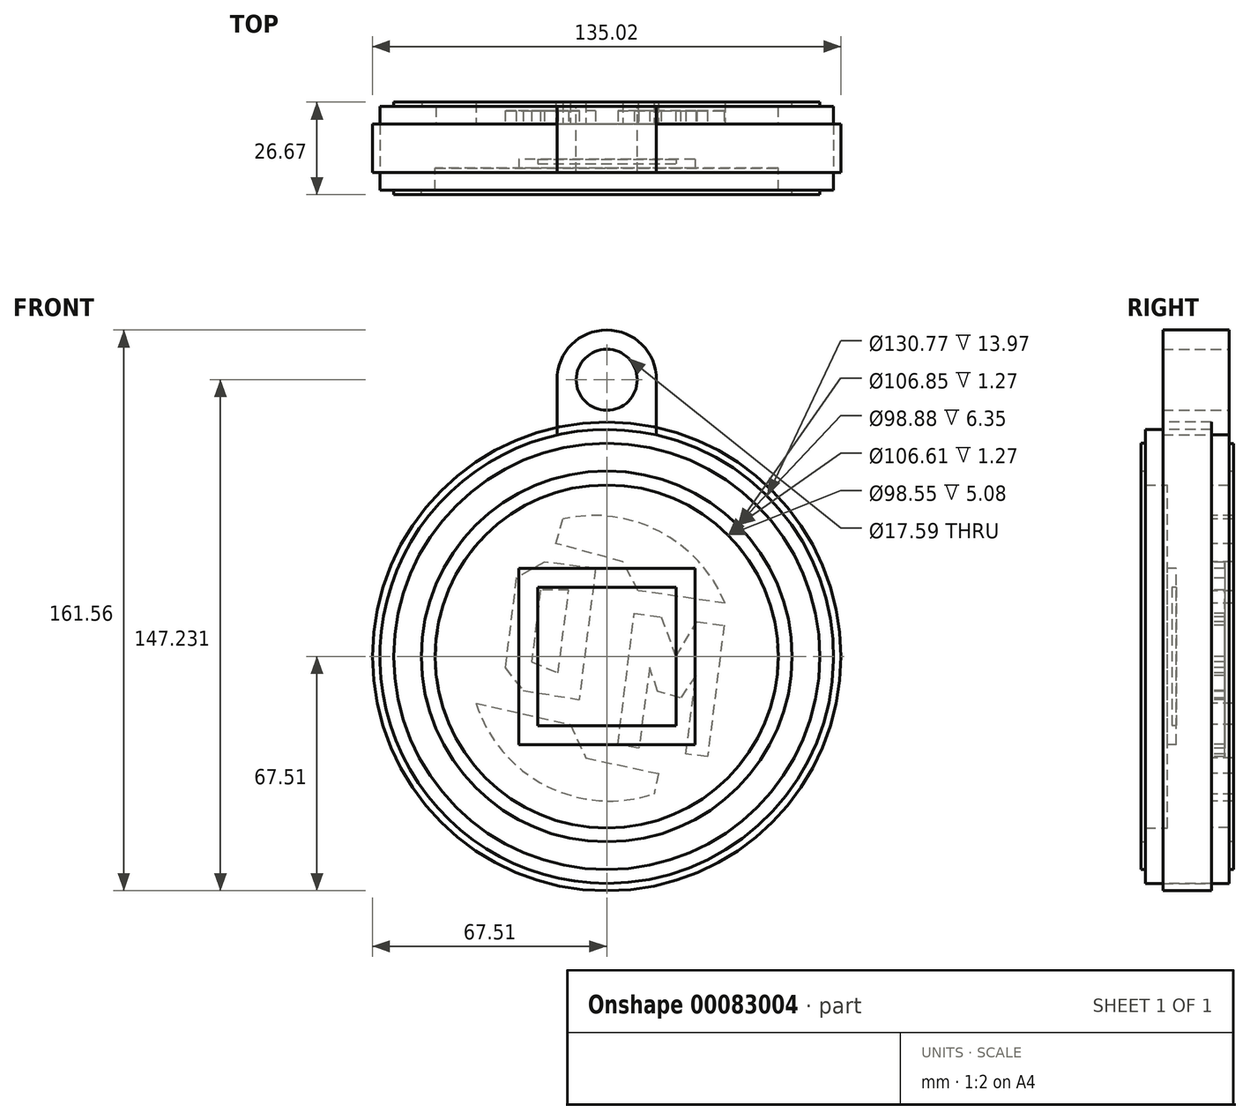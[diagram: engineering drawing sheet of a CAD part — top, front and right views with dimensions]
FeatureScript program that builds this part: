
annotation { "Feature Type Name" : "Feature", "Feature Type Description" : "" }
export const myFeature = defineFeature(function(context is Context, id is Id, definition is map)
    precondition{}
    {
        {
            var Q0;
            Q0=qCreatedBy(makeId("Front.planeOp"),FACE);
            var sketch = newSketch(context, id + "F0", { "sketchPlane" : qUnion([Q0])});
            skCircle(sketch, "E0", {"center": v(0, 0) * mm, "radius": 65.39 * mm});
            skCircle(sketch, "E1", {"center": v(0, 0) * mm, "radius": 49.28 * mm});
            skSolve(sketch);
        }
        {
            var Q0;
            Q0=makeQuery(id+"F0.imprint","IMPRINT",FACE,{"disambiguationData":[TD([[makeQuery(id+"F0.imprint","IMPRINT",EDGE,{"derivedFrom":sQuery(id+"F0.wireOp",EDGE,"E1")}),1.0]])]});
            var Q1;
            Q1=makeQuery(id+"F0.imprint","IMPRINT",FACE,{"disambiguationData":[TD([[makeQuery(id+"F0.imprint","IMPRINT",EDGE,{"derivedFrom":sQuery(id+"F0.wireOp",EDGE,"E0")}),1.0]])]});
            extrude(context, id + "F1", {"entities" : qUnion([Q0, Q1]), "depth" : 12.7 * mm});
        }
        {
            var Q0;
            Q0=makeQuery(id+"F0.imprint","IMPRINT",FACE,{"disambiguationData":[TD([[makeQuery(id+"F0.imprint","IMPRINT",EDGE,{"derivedFrom":sQuery(id+"F0.wireOp",EDGE,"E0")}),1.0]])]});
            extrude(context, id + "F2", {"entities" : qUnion([Q0]), "operationType" : NewBodyOperationType.ADD, "oppositeDirection" : true, "depth" : 5.08 * mm});
        }
        {
            var Q0;
            Q0=makeQuery(id+"F1.opExtrude","CAP_FACE",FACE,{"disambiguationData":[OSD([sQuery(id+"F0.wireOp",EDGE,"E0")])],"isStart":false});
            var sketch = newSketch(context, id + "F3", { "sketchPlane" : qUnion([Q0])});
            skCircle(sketch, "E2", {"center": v(0, 0) * mm, "radius": 49.44 * mm});
            skSolve(sketch);
        }
        {
            var Q0;
            Q0=makeQuery(id+"F3.imprint","IMPRINT",FACE,{"disambiguationData":[TD([[makeQuery(id+"F3.imprint","IMPRINT",EDGE,{"derivedFrom":sQuery(id+"F3.wireOp",EDGE,"E2")}),-1.0]])]});
            extrude(context, id + "F4", {"entities" : qUnion([Q0]), "operationType" : NewBodyOperationType.ADD, "depth" : 6.35 * mm});
        }
        {
            var Q0;
            Q0=makeQuery(id+"F4.opExtrude","CAP_FACE",FACE,{"disambiguationData":[OSD([sQuery(id+"F0.wireOp",EDGE,"E0"),sQuery(id+"F3.wireOp",EDGE,"E2")])],"isStart":false});
            var sketch = newSketch(context, id + "F5", { "sketchPlane" : qUnion([Q0])});
            skLineSegment(sketch, "E3", {"start": v(0, 49.44) * mm, "end": v(0, 65.39) * mm});
            skPoint(sketch, "E4", {"position": v(0, 57.41) * mm});
            skLineSegment(sketch, "E5", {"start": v(0, 57.41) * mm, "end": v(0, 65.39) * mm});
            skLineSegment(sketch, "E6", {"start": v(0, 49.44) * mm, "end": v(0, 57.41) * mm});
            skPoint(sketch, "E7", {"position": v(0, 53.43) * mm});
            skPoint(sketch, "E8", {"position": v(0, 61.4) * mm});
            skCircle(sketch, "E9", {"center": v(0, 0) * mm, "radius": 53.43 * mm});
            skCircle(sketch, "E10", {"center": v(0, 0) * mm, "radius": 61.4 * mm});
            skSolve(sketch);
        }
        {
            var Q0;
            Q0=makeQuery(id+"F5.imprint","IMPRINT",FACE,{"disambiguationData":[TD([[makeQuery(id+"F5.imprint","IMPRINT",EDGE,{"derivedFrom":sQuery(id+"F5.wireOp",EDGE,"E9")}),-1.0]])]});
            extrude(context, id + "F6", {"entities" : qUnion([Q0]), "operationType" : NewBodyOperationType.ADD, "depth" : 1.27 * mm});
        }
        {
            var Q0;
            Q0=makeQuery(id+"F2.opExtrude","CAP_FACE",FACE,{"disambiguationData":[OSD([sQuery(id+"F0.wireOp",EDGE,"E0"),sQuery(id+"F0.wireOp",EDGE,"E1")])],"isStart":false});
            var sketch = newSketch(context, id + "F7", { "sketchPlane" : qUnion([Q0])});
            skLineSegment(sketch, "E11", {"start": v(0, 49.28) * mm, "end": v(0, 65.39) * mm});
            skPoint(sketch, "E12", {"position": v(0, 57.33) * mm});
            skLineSegment(sketch, "E13", {"start": v(0, 57.33) * mm, "end": v(0, 65.39) * mm});
            skLineSegment(sketch, "E14", {"start": v(0, 57.33) * mm, "end": v(0, 49.28) * mm});
            skPoint(sketch, "E15", {"position": v(0, 61.36) * mm});
            skPoint(sketch, "E16", {"position": v(0, 53.3) * mm});
            skCircle(sketch, "E17", {"center": v(0, 0) * mm, "radius": 53.3 * mm});
            skCircle(sketch, "E18", {"center": v(0, 0) * mm, "radius": 61.36 * mm});
            skSolve(sketch);
        }
        {
            var Q0;
            Q0=makeQuery(id+"F7.imprint","IMPRINT",FACE,{"disambiguationData":[TD([[makeQuery(id+"F7.imprint","IMPRINT",EDGE,{"derivedFrom":sQuery(id+"F7.wireOp",EDGE,"E17")}),-1.0]])]});
            extrude(context, id + "F8", {"entities" : qUnion([Q0]), "operationType" : NewBodyOperationType.ADD, "depth" : 1.27 * mm});
        }
        {
            var Q0;
            Q0=makeQuery(id+"F0.imprint","IMPRINT",FACE,{"disambiguationData":[TD([[makeQuery(id+"F0.imprint","IMPRINT",EDGE,{"derivedFrom":sQuery(id+"F0.wireOp",EDGE,"E1")}),1.0]])]});
            var sketch = newSketch(context, id + "F9", { "sketchPlane" : qUnion([Q0])});
            skLineSegment(sketch, "E19", {"start": v(0, 0) * mm, "end": v(6.38, 0) * mm});
            skLineSegment(sketch, "E20", {"start": v(0, 0) * mm, "end": v(-6.38, 0) * mm});
            skLineSegment(sketch, "E21", {"start": v(6.38, 0) * mm, "end": v(3.19, -25.35) * mm});
            skPoint(sketch, "E21.endSnap0", {"position": v(3.19, 0) * mm});
            skLineSegment(sketch, "E22", {"start": v(-6.38, 0) * mm, "end": v(-3.19, 25.35) * mm});
            skPoint(sketch, "E22.endSnap0", {"position": v(-3.19, 0) * mm});
            skLineSegment(sketch, "E23", {"start": v(6.38, 0) * mm, "end": v(7.93, 12.37) * mm});
            skLineSegment(sketch, "E24", {"start": v(-6.38, 0) * mm, "end": v(-7.94, -12.42) * mm});
            skLineSegment(sketch, "E25", {"start": v(7.93, 12.37) * mm, "end": v(15.7, 11.4) * mm});
            skLineSegment(sketch, "E26", {"start": v(15.7, 11.4) * mm, "end": v(19.92, 0) * mm});
            skLineSegment(sketch, "E27", {"start": v(19.92, 0) * mm, "end": v(25.93, 10) * mm});
            skLineSegment(sketch, "E28", {"start": v(25.93, 10) * mm, "end": v(33.82, 9) * mm});
            skLineSegment(sketch, "E29", {"start": v(33.82, 9) * mm, "end": v(29.05, -28.9) * mm});
            skLineSegment(sketch, "E30", {"start": v(29.05, -28.9) * mm, "end": v(22.84, -28.11) * mm});
            skLineSegment(sketch, "E31", {"start": v(22.84, -28.11) * mm, "end": v(25.68, -5.55) * mm});
            skLineSegment(sketch, "E32", {"start": v(25.68, -5.55) * mm, "end": v(21.28, -11.93) * mm});
            skLineSegment(sketch, "E33", {"start": v(21.28, -11.93) * mm, "end": v(14.68, -10) * mm});
            skLineSegment(sketch, "E34", {"start": v(14.68, -10) * mm, "end": v(12.35, -3.2) * mm});
            skLineSegment(sketch, "E35", {"start": v(12.35, -3.2) * mm, "end": v(9.24, -26.49) * mm});
            skLineSegment(sketch, "E36", {"start": v(9.24, -26.49) * mm, "end": v(3.19, -25.35) * mm});
            skLineSegment(sketch, "E37", {"start": v(-3.19, 25.35) * mm, "end": v(-17.93, 27.2) * mm});
            skLineSegment(sketch, "E38", {"start": v(-17.93, 27.2) * mm, "end": v(-26.08, 22.6) * mm});
            skLineSegment(sketch, "E39", {"start": v(-26.08, 22.6) * mm, "end": v(-29.33, -3.23) * mm});
            skLineSegment(sketch, "E40", {"start": v(-29.33, -3.23) * mm, "end": v(-24.14, -9.8) * mm});
            skLineSegment(sketch, "E41", {"start": v(-24.14, -9.8) * mm, "end": v(-7.94, -12.42) * mm});
            skLineSegment(sketch, "E42", {"start": v(-10.94, 19.12) * mm, "end": v(-19.09, 19.12) * mm});
            skLineSegment(sketch, "E43", {"start": v(-19.09, 19.12) * mm, "end": v(-21.68, -1.5) * mm});
            skLineSegment(sketch, "E44", {"start": v(-21.68, -1.5) * mm, "end": v(-14.04, -4.75) * mm});
            skLineSegment(sketch, "E45", {"start": v(-14.04, -4.75) * mm, "end": v(-10.94, 19.12) * mm});
            skSolve(sketch);
        }
        {
            var Q0;
            Q0 = qSketchRegion(id + "F9", true);
            extrude(context, id + "F10", {"entities" : qUnion([Q0]), "operationType" : NewBodyOperationType.ADD, "oppositeDirection" : true, "depth" : 3.8 * mm});
        }
        {
            var Q0;
            Q0=makeQuery(id+"F1.opExtrude","CAP_FACE",FACE,{"disambiguationData":[OSD([sQuery(id+"F0.wireOp",EDGE,"E0")])],"isStart":false});
            var sketch = newSketch(context, id + "F11", { "sketchPlane" : qUnion([Q0])});
            skLineSegment(sketch, "E46.bottom", {"start": v(0, 0) * mm, "end": v(-25.4, 0) * mm});
            skLineSegment(sketch, "E46.top", {"start": v(0, 25.4) * mm, "end": v(-25.4, 25.4) * mm});
            skLineSegment(sketch, "E46.left", {"start": v(0, 0) * mm, "end": v(0, 25.4) * mm});
            skLineSegment(sketch, "E46.right", {"start": v(-25.4, 0) * mm, "end": v(-25.4, 25.4) * mm});
            skLineSegment(sketch, "E47.MirrorCS", {"start": v(25.4, 0) * mm, "end": v(25.4, 25.4) * mm});
            skLineSegment(sketch, "E48.MirrorCS", {"start": v(0, 25.4) * mm, "end": v(25.4, 25.4) * mm});
            skLineSegment(sketch, "E49.MirrorCS", {"start": v(0, 0) * mm, "end": v(25.4, 0) * mm});
            skLineSegment(sketch, "E50.MirrorCS", {"start": v(-25.4, 0) * mm, "end": v(-25.4, -25.4) * mm});
            skLineSegment(sketch, "E51.MirrorCS", {"start": v(0, -25.4) * mm, "end": v(-25.4, -25.4) * mm});
            skLineSegment(sketch, "E52.MirrorCS", {"start": v(0, -25.4) * mm, "end": v(25.4, -25.4) * mm});
            skLineSegment(sketch, "E53.MirrorCS", {"start": v(25.4, 0) * mm, "end": v(25.4, -25.4) * mm});
            skLineSegment(sketch, "E54.MirrorCS", {"start": v(0, 0) * mm, "end": v(0, -25.4) * mm});
            skPoint(sketch, "E55", {"position": v(-12.7, 12.7) * mm});
            skPoint(sketch, "E55.positionSnap0", {"position": v(-25.4, 12.7) * mm});
            skPoint(sketch, "E55.positionSnap1", {"position": v(-12.7, 25.4) * mm});
            skPoint(sketch, "E56", {"position": v(12.7, 12.7) * mm});
            skPoint(sketch, "E56.positionSnap0", {"position": v(25.4, 12.7) * mm});
            skPoint(sketch, "E56.positionSnap1", {"position": v(12.7, 25.4) * mm});
            skPoint(sketch, "E57", {"position": v(-12.7, -12.7) * mm});
            skPoint(sketch, "E57.positionSnap0", {"position": v(-12.7, -25.4) * mm});
            skPoint(sketch, "E57.positionSnap1", {"position": v(0, -12.7) * mm});
            skPoint(sketch, "E58", {"position": v(12.7, -12.7) * mm});
            skPoint(sketch, "E58.positionSnap0", {"position": v(12.7, -25.4) * mm});
            skPoint(sketch, "E58.positionSnap1", {"position": v(25.4, -12.7) * mm});
            skLineSegment(sketch, "E59.bottom", {"start": v(-12.7, 12.7) * mm, "end": v(12.7, 12.7) * mm});
            skLineSegment(sketch, "E59.top", {"start": v(-12.7, -12.7) * mm, "end": v(12.7, -12.7) * mm});
            skLineSegment(sketch, "E59.left", {"start": v(-12.7, 12.7) * mm, "end": v(-12.7, -12.7) * mm});
            skLineSegment(sketch, "E59.right", {"start": v(12.7, 12.7) * mm, "end": v(12.7, -12.7) * mm});
            skLineSegment(sketch, "E60", {"start": v(-12.7, 12.7) * mm, "end": v(-12.7, 25.4) * mm});
            skLineSegment(sketch, "E61", {"start": v(-25.4, 12.7) * mm, "end": v(-12.7, 12.7) * mm});
            skLineSegment(sketch, "E62", {"start": v(12.7, 12.7) * mm, "end": v(12.7, 25.4) * mm});
            skLineSegment(sketch, "E63", {"start": v(12.7, 12.7) * mm, "end": v(25.4, 12.7) * mm});
            skLineSegment(sketch, "E64", {"start": v(12.7, -25.4) * mm, "end": v(12.7, -12.7) * mm});
            skLineSegment(sketch, "E65", {"start": v(12.7, -12.7) * mm, "end": v(25.4, -12.7) * mm});
            skLineSegment(sketch, "E66", {"start": v(-12.7, -12.7) * mm, "end": v(-12.7, -25.4) * mm});
            skLineSegment(sketch, "E67", {"start": v(-12.7, -12.7) * mm, "end": v(-25.4, -12.7) * mm});
            skPoint(sketch, "E68", {"position": v(-19.05, 19.05) * mm});
            skPoint(sketch, "E68.positionSnap0", {"position": v(-12.7, 19.05) * mm});
            skPoint(sketch, "E68.positionSnap1", {"position": v(-19.05, 12.7) * mm});
            skPoint(sketch, "E69", {"position": v(19.05, 19.05) * mm});
            skPoint(sketch, "E69.positionSnap0", {"position": v(12.7, 19.05) * mm});
            skPoint(sketch, "E69.positionSnap1", {"position": v(19.05, 12.7) * mm});
            skPoint(sketch, "E70", {"position": v(-19.05, -19.05) * mm});
            skPoint(sketch, "E70.positionSnap0", {"position": v(-19.05, -12.7) * mm});
            skPoint(sketch, "E70.positionSnap1", {"position": v(-12.7, -19.05) * mm});
            skPoint(sketch, "E71", {"position": v(19.05, -19.05) * mm});
            skPoint(sketch, "E71.positionSnap0", {"position": v(19.05, -12.7) * mm});
            skPoint(sketch, "E71.positionSnap1", {"position": v(12.7, -19.05) * mm});
            skLineSegment(sketch, "E72.bottom", {"start": v(-19.05, 19.05) * mm, "end": v(19.05, 19.05) * mm});
            skLineSegment(sketch, "E72.top", {"start": v(-19.05, -19.05) * mm, "end": v(19.05, -19.05) * mm});
            skLineSegment(sketch, "E72.left", {"start": v(-19.05, 19.05) * mm, "end": v(-19.05, -19.05) * mm});
            skLineSegment(sketch, "E72.right", {"start": v(19.05, 19.05) * mm, "end": v(19.05, -19.05) * mm});
            skSolve(sketch);
        }
        {
            var Q0;
            {var subQ1=sQuery(id+"F11.wireOp",EDGE,"E46.right");var subQ6=sQuery(id+"F11.wireOp",EDGE,"E46.top");var subQ10=makeQuery(id+"F11.imprint","INTERSECT",VERTEX,{"derivedFrom":[subQ6,subQ1]});Q0=makeQuery(id+"F11.imprint","IMPRINT",FACE,{"disambiguationData":[TD([[makeQuery(id+"F11.imprint","IMPRINT",EDGE,{"disambiguationData":[TD([[subQ10,1.0]])],"derivedFrom":subQ6}),1.0]])]});}
            var Q1;
            {var subQ3=sQuery(id+"F11.wireOp",EDGE,"E72.bottom");var subQ5=sQuery(id+"F11.wireOp",EDGE,"E72.left");var subQ6=makeQuery(id+"F11.imprint","INTERSECT",VERTEX,{"derivedFrom":[subQ3,subQ5]});Q1=makeQuery(id+"F11.imprint","IMPRINT",FACE,{"disambiguationData":[TD([[makeQuery(id+"F11.imprint","IMPRINT",EDGE,{"disambiguationData":[TD([[subQ6,-1.0]])],"derivedFrom":subQ3}),-1.0]])]});}
            var Q2;
            {var subQ0=sQuery(id+"F11.wireOp",EDGE,"E59.bottom");var subQ1=sQuery(id+"F11.wireOp",EDGE,"E46.left");var subQ2=makeQuery(id+"F11.imprint","INTERSECT",VERTEX,{"derivedFrom":[subQ1,subQ0]});Q2=makeQuery(id+"F11.imprint","IMPRINT",FACE,{"disambiguationData":[TD([[makeQuery(id+"F11.imprint","IMPRINT",EDGE,{"disambiguationData":[TD([[subQ2,-1.0]])],"derivedFrom":subQ1}),-1.0]])]});}
            var Q3;
            {var subQ0=sQuery(id+"F11.wireOp",EDGE,"E48.MirrorCS");var subQ5=sQuery(id+"F11.wireOp",EDGE,"E62");var subQ6=makeQuery(id+"F11.imprint","INTERSECT",VERTEX,{"derivedFrom":[subQ0,subQ5]});Q3=makeQuery(id+"F11.imprint","IMPRINT",FACE,{"disambiguationData":[TD([[makeQuery(id+"F11.imprint","IMPRINT",EDGE,{"disambiguationData":[TD([[subQ6,1.0]])],"derivedFrom":subQ5}),1.0]])]});}
            var Q4;
            {var subQ1=sQuery(id+"F11.wireOp",EDGE,"E46.top");var subQ3=sQuery(id+"F11.wireOp",EDGE,"E60");var subQ4=makeQuery(id+"F11.imprint","INTERSECT",VERTEX,{"derivedFrom":[subQ1,subQ3]});Q4=makeQuery(id+"F11.imprint","IMPRINT",FACE,{"disambiguationData":[TD([[makeQuery(id+"F11.imprint","IMPRINT",EDGE,{"disambiguationData":[TD([[subQ4,1.0]])],"derivedFrom":subQ3}),-1.0]])]});}
            var Q5;
            {var subQ0=sQuery(id+"F11.wireOp",EDGE,"E59.bottom");var subQ1=sQuery(id+"F11.wireOp",EDGE,"E46.left");var subQ2=makeQuery(id+"F11.imprint","INTERSECT",VERTEX,{"derivedFrom":[subQ1,subQ0]});Q5=makeQuery(id+"F11.imprint","IMPRINT",FACE,{"disambiguationData":[TD([[makeQuery(id+"F11.imprint","IMPRINT",EDGE,{"disambiguationData":[TD([[subQ2,-1.0]])],"derivedFrom":subQ1}),1.0]])]});}
            var Q6;
            {var subQ1=sQuery(id+"F11.wireOp",EDGE,"E46.bottom");var subQ3=sQuery(id+"F11.wireOp",EDGE,"E59.left");var subQ4=makeQuery(id+"F11.imprint","INTERSECT",VERTEX,{"derivedFrom":[subQ1,subQ3]});Q6=makeQuery(id+"F11.imprint","IMPRINT",FACE,{"disambiguationData":[TD([[makeQuery(id+"F11.imprint","IMPRINT",EDGE,{"disambiguationData":[TD([[subQ4,1.0]])],"derivedFrom":subQ1}),-1.0]])]});}
            var Q7;
            {var subQ0=sQuery(id+"F11.wireOp",EDGE,"E59.left");var subQ1=sQuery(id+"F11.wireOp",EDGE,"E46.bottom");var subQ2=makeQuery(id+"F11.imprint","INTERSECT",VERTEX,{"derivedFrom":[subQ1,subQ0]});Q7=makeQuery(id+"F11.imprint","IMPRINT",FACE,{"disambiguationData":[TD([[makeQuery(id+"F11.imprint","IMPRINT",EDGE,{"disambiguationData":[TD([[subQ2,-1.0]])],"derivedFrom":subQ1}),-1.0]])]});}
            var Q8;
            {var subQ0=sQuery(id+"F11.wireOp",EDGE,"E46.right");var subQ5=sQuery(id+"F11.wireOp",EDGE,"E61");var subQ6=makeQuery(id+"F11.imprint","INTERSECT",VERTEX,{"derivedFrom":[subQ0,subQ5]});Q8=makeQuery(id+"F11.imprint","IMPRINT",FACE,{"disambiguationData":[TD([[makeQuery(id+"F11.imprint","IMPRINT",EDGE,{"disambiguationData":[TD([[subQ6,-1.0]])],"derivedFrom":subQ5}),-1.0]])]});}
            var Q9;
            {var subQ0=sQuery(id+"F11.wireOp",EDGE,"E50.MirrorCS");var subQ5=sQuery(id+"F11.wireOp",EDGE,"E67");var subQ6=makeQuery(id+"F11.imprint","INTERSECT",VERTEX,{"derivedFrom":[subQ0,subQ5]});Q9=makeQuery(id+"F11.imprint","IMPRINT",FACE,{"disambiguationData":[TD([[makeQuery(id+"F11.imprint","IMPRINT",EDGE,{"disambiguationData":[TD([[subQ6,1.0]])],"derivedFrom":subQ5}),-1.0]])]});}
            var Q10;
            {var subQ0=sQuery(id+"F11.wireOp",EDGE,"E59.left");var subQ1=sQuery(id+"F11.wireOp",EDGE,"E46.bottom");var subQ2=makeQuery(id+"F11.imprint","INTERSECT",VERTEX,{"derivedFrom":[subQ1,subQ0]});Q10=makeQuery(id+"F11.imprint","IMPRINT",FACE,{"disambiguationData":[TD([[makeQuery(id+"F11.imprint","IMPRINT",EDGE,{"disambiguationData":[TD([[subQ2,-1.0]])],"derivedFrom":subQ1}),1.0]])]});}
            var Q11;
            {var subQ1=sQuery(id+"F11.wireOp",EDGE,"E46.bottom");var subQ3=sQuery(id+"F11.wireOp",EDGE,"E59.left");var subQ4=makeQuery(id+"F11.imprint","INTERSECT",VERTEX,{"derivedFrom":[subQ1,subQ3]});Q11=makeQuery(id+"F11.imprint","IMPRINT",FACE,{"disambiguationData":[TD([[makeQuery(id+"F11.imprint","IMPRINT",EDGE,{"disambiguationData":[TD([[subQ4,1.0]])],"derivedFrom":subQ1}),1.0]])]});}
            var Q12;
            {var subQ1=sQuery(id+"F11.wireOp",EDGE,"E49.MirrorCS");var subQ3=sQuery(id+"F11.wireOp",EDGE,"E59.right");var subQ4=makeQuery(id+"F11.imprint","INTERSECT",VERTEX,{"derivedFrom":[subQ1,subQ3]});Q12=makeQuery(id+"F11.imprint","IMPRINT",FACE,{"disambiguationData":[TD([[makeQuery(id+"F11.imprint","IMPRINT",EDGE,{"disambiguationData":[TD([[subQ4,1.0]])],"derivedFrom":subQ1}),-1.0]])]});}
            var Q13;
            {var subQ1=sQuery(id+"F11.wireOp",EDGE,"E46.left");var subQ3=sQuery(id+"F11.wireOp",EDGE,"E59.bottom");var subQ4=makeQuery(id+"F11.imprint","INTERSECT",VERTEX,{"derivedFrom":[subQ1,subQ3]});Q13=makeQuery(id+"F11.imprint","IMPRINT",FACE,{"disambiguationData":[TD([[makeQuery(id+"F11.imprint","IMPRINT",EDGE,{"disambiguationData":[TD([[subQ4,1.0]])],"derivedFrom":subQ1}),-1.0]])]});}
            var Q14;
            {var subQ0=sQuery(id+"F11.wireOp",EDGE,"E59.right");var subQ1=sQuery(id+"F11.wireOp",EDGE,"E49.MirrorCS");var subQ2=makeQuery(id+"F11.imprint","INTERSECT",VERTEX,{"derivedFrom":[subQ1,subQ0]});Q14=makeQuery(id+"F11.imprint","IMPRINT",FACE,{"disambiguationData":[TD([[makeQuery(id+"F11.imprint","IMPRINT",EDGE,{"disambiguationData":[TD([[subQ2,-1.0]])],"derivedFrom":subQ1}),1.0]])]});}
            var Q15;
            {var subQ1=sQuery(id+"F11.wireOp",EDGE,"E47.MirrorCS");var subQ3=sQuery(id+"F11.wireOp",EDGE,"E63");var subQ4=makeQuery(id+"F11.imprint","INTERSECT",VERTEX,{"derivedFrom":[subQ1,subQ3]});Q15=makeQuery(id+"F11.imprint","IMPRINT",FACE,{"disambiguationData":[TD([[makeQuery(id+"F11.imprint","IMPRINT",EDGE,{"disambiguationData":[TD([[subQ4,1.0]])],"derivedFrom":subQ3}),-1.0]])]});}
            var Q16;
            {var subQ1=sQuery(id+"F11.wireOp",EDGE,"E47.MirrorCS");var subQ5=sQuery(id+"F11.wireOp",EDGE,"E48.MirrorCS");var subQ6=makeQuery(id+"F11.imprint","INTERSECT",VERTEX,{"derivedFrom":[subQ1,subQ5]});Q16=makeQuery(id+"F11.imprint","IMPRINT",FACE,{"disambiguationData":[TD([[makeQuery(id+"F11.imprint","IMPRINT",EDGE,{"disambiguationData":[TD([[subQ6,1.0]])],"derivedFrom":subQ1}),1.0]])]});}
            var Q17;
            {var subQ3=sQuery(id+"F11.wireOp",EDGE,"E72.bottom");var subQ5=sQuery(id+"F11.wireOp",EDGE,"E72.right");var subQ7=makeQuery(id+"F11.imprint","INTERSECT",VERTEX,{"derivedFrom":[subQ3,subQ5]});Q17=makeQuery(id+"F11.imprint","IMPRINT",FACE,{"disambiguationData":[TD([[makeQuery(id+"F11.imprint","IMPRINT",EDGE,{"disambiguationData":[TD([[subQ7,1.0]])],"derivedFrom":subQ3}),-1.0]])]});}
            var Q18;
            {var subQ0=sQuery(id+"F11.wireOp",EDGE,"E59.right");var subQ1=sQuery(id+"F11.wireOp",EDGE,"E49.MirrorCS");var subQ2=makeQuery(id+"F11.imprint","INTERSECT",VERTEX,{"derivedFrom":[subQ1,subQ0]});Q18=makeQuery(id+"F11.imprint","IMPRINT",FACE,{"disambiguationData":[TD([[makeQuery(id+"F11.imprint","IMPRINT",EDGE,{"disambiguationData":[TD([[subQ2,-1.0]])],"derivedFrom":subQ1}),-1.0]])]});}
            var Q19;
            {var subQ0=sQuery(id+"F11.wireOp",EDGE,"E53.MirrorCS");var subQ5=sQuery(id+"F11.wireOp",EDGE,"E65");var subQ6=makeQuery(id+"F11.imprint","INTERSECT",VERTEX,{"derivedFrom":[subQ0,subQ5]});Q19=makeQuery(id+"F11.imprint","IMPRINT",FACE,{"disambiguationData":[TD([[makeQuery(id+"F11.imprint","IMPRINT",EDGE,{"disambiguationData":[TD([[subQ6,1.0]])],"derivedFrom":subQ5}),1.0]])]});}
            var Q20;
            {var subQ3=sQuery(id+"F11.wireOp",EDGE,"E72.top");var subQ5=sQuery(id+"F11.wireOp",EDGE,"E72.right");var subQ6=makeQuery(id+"F11.imprint","INTERSECT",VERTEX,{"derivedFrom":[subQ3,subQ5]});Q20=makeQuery(id+"F11.imprint","IMPRINT",FACE,{"disambiguationData":[TD([[makeQuery(id+"F11.imprint","IMPRINT",EDGE,{"disambiguationData":[TD([[subQ6,1.0]])],"derivedFrom":subQ3}),1.0]])]});}
            var Q21;
            {var subQ0=sQuery(id+"F11.wireOp",EDGE,"E59.top");var subQ1=sQuery(id+"F11.wireOp",EDGE,"E54.MirrorCS");var subQ2=makeQuery(id+"F11.imprint","INTERSECT",VERTEX,{"derivedFrom":[subQ1,subQ0]});Q21=makeQuery(id+"F11.imprint","IMPRINT",FACE,{"disambiguationData":[TD([[makeQuery(id+"F11.imprint","IMPRINT",EDGE,{"disambiguationData":[TD([[subQ2,-1.0]])],"derivedFrom":subQ1}),1.0]])]});}
            var Q22;
            {var subQ0=sQuery(id+"F11.wireOp",EDGE,"E59.top");var subQ1=sQuery(id+"F11.wireOp",EDGE,"E54.MirrorCS");var subQ2=makeQuery(id+"F11.imprint","INTERSECT",VERTEX,{"derivedFrom":[subQ1,subQ0]});Q22=makeQuery(id+"F11.imprint","IMPRINT",FACE,{"disambiguationData":[TD([[makeQuery(id+"F11.imprint","IMPRINT",EDGE,{"disambiguationData":[TD([[subQ2,-1.0]])],"derivedFrom":subQ1}),-1.0]])]});}
            var Q23;
            {var subQ3=sQuery(id+"F11.wireOp",EDGE,"E72.top");var subQ5=sQuery(id+"F11.wireOp",EDGE,"E72.left");var subQ6=makeQuery(id+"F11.imprint","INTERSECT",VERTEX,{"derivedFrom":[subQ3,subQ5]});Q23=makeQuery(id+"F11.imprint","IMPRINT",FACE,{"disambiguationData":[TD([[makeQuery(id+"F11.imprint","IMPRINT",EDGE,{"disambiguationData":[TD([[subQ6,-1.0]])],"derivedFrom":subQ3}),1.0]])]});}
            var Q24;
            {var subQ1=sQuery(id+"F11.wireOp",EDGE,"E50.MirrorCS");var subQ6=sQuery(id+"F11.wireOp",EDGE,"E51.MirrorCS");var subQ11=makeQuery(id+"F11.imprint","INTERSECT",VERTEX,{"derivedFrom":[subQ1,subQ6]});Q24=makeQuery(id+"F11.imprint","IMPRINT",FACE,{"disambiguationData":[TD([[makeQuery(id+"F11.imprint","IMPRINT",EDGE,{"disambiguationData":[TD([[subQ11,1.0]])],"derivedFrom":subQ1}),1.0]])]});}
            var Q25;
            {var subQ1=sQuery(id+"F11.wireOp",EDGE,"E51.MirrorCS");var subQ3=sQuery(id+"F11.wireOp",EDGE,"E66");var subQ4=makeQuery(id+"F11.imprint","INTERSECT",VERTEX,{"derivedFrom":[subQ1,subQ3]});Q25=makeQuery(id+"F11.imprint","IMPRINT",FACE,{"disambiguationData":[TD([[makeQuery(id+"F11.imprint","IMPRINT",EDGE,{"disambiguationData":[TD([[subQ4,1.0]])],"derivedFrom":subQ3}),1.0]])]});}
            var Q26;
            {var subQ1=sQuery(id+"F11.wireOp",EDGE,"E52.MirrorCS");var subQ3=sQuery(id+"F11.wireOp",EDGE,"E64");var subQ4=makeQuery(id+"F11.imprint","INTERSECT",VERTEX,{"derivedFrom":[subQ1,subQ3]});Q26=makeQuery(id+"F11.imprint","IMPRINT",FACE,{"disambiguationData":[TD([[makeQuery(id+"F11.imprint","IMPRINT",EDGE,{"disambiguationData":[TD([[subQ4,-1.0]])],"derivedFrom":subQ3}),1.0]])]});}
            var Q27;
            {var subQ1=sQuery(id+"F11.wireOp",EDGE,"E53.MirrorCS");var subQ5=sQuery(id+"F11.wireOp",EDGE,"E52.MirrorCS");var subQ6=makeQuery(id+"F11.imprint","INTERSECT",VERTEX,{"derivedFrom":[subQ5,subQ1]});Q27=makeQuery(id+"F11.imprint","IMPRINT",FACE,{"disambiguationData":[TD([[makeQuery(id+"F11.imprint","IMPRINT",EDGE,{"disambiguationData":[TD([[subQ6,1.0]])],"derivedFrom":subQ5}),1.0]])]});}
            extrude(context, id + "F12", {"entities" : qUnion([Q0, Q1, Q2, Q3, Q4, Q5, Q6, Q7, Q8, Q9, Q10, Q11, Q12, Q13, Q14, Q15, Q16, Q17, Q18, Q19, Q20, Q21, Q22, Q23, Q24, Q25, Q26, Q27]), "operationType" : NewBodyOperationType.REMOVE, "oppositeDirection" : true, "depth" : 1.27 * mm});
        }
        {
            var Q0;
            Q0=makeQuery(id+"F12.boolean.opBoolean","COPY",FACE,{"derivedFrom":makeQuery(id+"F12.opExtrude","CAP_FACE",FACE,{"disambiguationData":[OSD([sQuery(id+"F11.wireOp",EDGE,"E46.top"),sQuery(id+"F11.wireOp",EDGE,"E46.right"),sQuery(id+"F11.wireOp",EDGE,"E47.MirrorCS"),sQuery(id+"F11.wireOp",EDGE,"E48.MirrorCS"),sQuery(id+"F11.wireOp",EDGE,"E50.MirrorCS"),sQuery(id+"F11.wireOp",EDGE,"E51.MirrorCS"),sQuery(id+"F11.wireOp",EDGE,"E52.MirrorCS"),sQuery(id+"F11.wireOp",EDGE,"E53.MirrorCS")])],"isStart":false})});
            var sketch = newSketch(context, id + "F13", { "sketchPlane" : qUnion([Q0])});
            skLineSegment(sketch, "E73", {"start": v(-25.4, 25.4) * mm, "end": v(25.4, -25.4) * mm});
            skLineSegment(sketch, "E74", {"start": v(-25.4, 25.4) * mm, "end": v(-19.95, 19.95) * mm});
            skLineSegment(sketch, "E75", {"start": v(25.4, -25.4) * mm, "end": v(19.96, -19.96) * mm});
            skLineSegment(sketch, "E76.bottom", {"start": v(-19.95, 19.95) * mm, "end": v(19.96, 19.95) * mm});
            skLineSegment(sketch, "E76.top", {"start": v(-19.95, -19.96) * mm, "end": v(19.96, -19.96) * mm});
            skLineSegment(sketch, "E76.left", {"start": v(-19.95, 19.95) * mm, "end": v(-19.95, -19.96) * mm});
            skLineSegment(sketch, "E76.right", {"start": v(19.96, 19.95) * mm, "end": v(19.96, -19.96) * mm});
            skSolve(sketch);
        }
        {
            var Q0;
            Q0=makeQuery(id+"F13.imprint","IMPRINT",FACE,{"disambiguationData":[TD([[makeQuery(id+"F13.imprint","IMPRINT",EDGE,{"derivedFrom":sQuery(id+"F13.wireOp",EDGE,"E73")}),1.0]])]});
            var Q1;
            Q1=makeQuery(id+"F13.imprint","IMPRINT",FACE,{"disambiguationData":[TD([[makeQuery(id+"F13.imprint","IMPRINT",EDGE,{"derivedFrom":sQuery(id+"F13.wireOp",EDGE,"E73")}),-1.0]])]});
            extrude(context, id + "F14", {"entities" : qUnion([Q0, Q1]), "operationType" : NewBodyOperationType.REMOVE, "oppositeDirection" : true, "depth" : 1.27 * mm});
        }
        {
            var Q0;
            Q0=makeQuery(id+"F0.imprint","IMPRINT",FACE,{"disambiguationData":[TD([[makeQuery(id+"F0.imprint","IMPRINT",EDGE,{"derivedFrom":sQuery(id+"F0.wireOp",EDGE,"E1")}),1.0]])]});
            var sketch = newSketch(context, id + "F15", { "sketchPlane" : qUnion([Q0])});
            skLineSegment(sketch, "E77", {"start": v(34.15, 15.3) * mm, "end": v(9.11, 18.96) * mm});
            skLineSegment(sketch, "E78", {"start": v(9.11, 18.96) * mm, "end": v(4.68, 27.3) * mm});
            skLineSegment(sketch, "E79", {"start": v(4.68, 27.3) * mm, "end": v(-14.62, 32.52) * mm});
            skLineSegment(sketch, "E80", {"start": v(-14.62, 32.52) * mm, "end": v(-12.7, 39.6) * mm});
            skArc(sketch, "E81", {"start": v(34.15, 15.3) * mm, "mid": v(15.17, 36.03) * mm, "end": v(-12.7, 39.6) * mm});
            skLineSegment(sketch, "E82", {"start": v(-31.05, -14.95) * mm, "end": v(-10.45, -19.64) * mm});
            skLineSegment(sketch, "E83", {"start": v(-10.45, -19.64) * mm, "end": v(-6.02, -29.3) * mm});
            skLineSegment(sketch, "E84", {"start": v(-6.02, -29.3) * mm, "end": v(14.85, -33.72) * mm});
            skLineSegment(sketch, "E85", {"start": v(14.85, -33.72) * mm, "end": v(13.6, -39.59) * mm});
            skLineSegment(sketch, "E86", {"start": v(-31.05, -14.95) * mm, "end": v(-37.67, -13.44) * mm});
            skArc(sketch, "E87", {"start": v(-37.67, -13.44) * mm, "mid": v(-17.5, -37.25) * mm, "end": v(13.6, -39.59) * mm});
            skSolve(sketch);
        }
        {
            var Q0;
            Q0 = qSketchRegion(id + "F15", true);
            extrude(context, id + "F16", {"entities" : qUnion([Q0]), "operationType" : NewBodyOperationType.ADD, "oppositeDirection" : true, "depth" : 6.35 * mm});
        }
        {
            var Q0;
            {var subQ0=sQuery(id+"F0.wireOp",EDGE,"E0");Q0=makeQuery(id+"F8.boolean.opBoolean","SPLIT",FACE,{"disambiguationData":[TD([makeQuery(id+"F1.opExtrude","SWEPT_FACE",FACE,{"disambiguationData":[OSD([subQ0])]})])],"derivedFrom":makeQuery(id+"F2.opExtrude","CAP_FACE",FACE,{"disambiguationData":[OSD([subQ0,sQuery(id+"F0.wireOp",EDGE,"E1")])],"isStart":false})});}
            var sketch = newSketch(context, id + "F17", { "sketchPlane" : qUnion([Q0])});
            skPoint(sketch, "E88", {"position": v(0, 65.39) * mm});
            skPoint(sketch, "E89", {"position": v(0, 79.72) * mm});
            skCircle(sketch, "E90", {"center": v(0, 79.72) * mm, "radius": 14.33 * mm});
            skPoint(sketch, "E91", {"position": v(-14.33, 79.72) * mm});
            skPoint(sketch, "E92", {"position": v(14.33, 79.72) * mm});
            skPoint(sketch, "E93", {"position": v(-14.33, 63.8) * mm});
            skPoint(sketch, "E94", {"position": v(14.33, 63.8) * mm});
            skLineSegment(sketch, "E95", {"start": v(-14.33, 79.72) * mm, "end": v(-14.33, 63.8) * mm});
            skLineSegment(sketch, "E96", {"start": v(14.33, 79.72) * mm, "end": v(14.33, 63.8) * mm});
            skCircle(sketch, "E97", {"center": v(0, 79.72) * mm, "radius": 8.8 * mm});
            skArc(sketch, "E98", {"start": v(14.33, 63.8) * mm, "mid": v(0, 65.39) * mm, "end": v(-14.33, 63.8) * mm});
            skSolve(sketch);
        }
        {
            var Q0;
            Q0=makeQuery(id+"F17.imprint","IMPRINT",FACE,{"disambiguationData":[TD([[makeQuery(id+"F17.imprint","IMPRINT",EDGE,{"derivedFrom":sQuery(id+"F17.wireOp",EDGE,"E97")}),-1.0]])]});
            var Q1;
            {var subQ0=sQuery(id+"F17.wireOp",EDGE,"E96");Q1=makeQuery(id+"F17.imprint","IMPRINT",FACE,{"disambiguationData":[TD([[makeQuery(id+"F17.imprint","IMPRINT",EDGE,{"derivedFrom":subQ0}),-1.0]])]});}
            var Q2;
            {var subQ0=sQuery(id+"F17.wireOp",EDGE,"E95");Q2=makeQuery(id+"F17.imprint","IMPRINT",FACE,{"disambiguationData":[TD([[makeQuery(id+"F17.imprint","IMPRINT",EDGE,{"derivedFrom":subQ0}),1.0]])]});}
            extrude(context, id + "F18", {"entities" : qUnion([Q0, Q1, Q2]), "operationType" : NewBodyOperationType.ADD, "oppositeDirection" : true, "depth" : 19.05 * mm});
        }
        {
            var Q0;
            Q0=makeQuery(id+"F18.opExtrude","SWEPT_FACE",FACE,{"disambiguationData":[OSD([sQuery(id+"F17.wireOp",EDGE,"E96")])]});
            var sketch = newSketch(context, id + "F19", { "sketchPlane" : qUnion([Q0])});
            skLineSegment(sketch, "E99", {"start": v(0, 63.8) * mm, "end": v(13.97, 63.8) * mm});
            skLineSegment(sketch, "E100", {"start": v(13.97, 63.8) * mm, "end": v(13.97, 65.97) * mm});
            skLineSegment(sketch, "E101.top", {"start": v(0, 65.97) * mm, "end": v(13.97, 65.97) * mm});
            skLineSegment(sketch, "E101.left", {"start": v(0, 63.8) * mm, "end": v(0, 65.97) * mm});
            skSolve(sketch);
        }
        {
            var Q0;
            Q0=makeQuery(id+"F19.imprint","IMPRINT",FACE,{"disambiguationData":[TD([[makeQuery(id+"F19.imprint","IMPRINT",EDGE,{"derivedFrom":sQuery(id+"F19.wireOp",EDGE,"E99")}),-1.0]])]});
            var Q1;
            Q1=makeQuery(id+"F8.opExtrude","CAP_EDGE",EDGE,{"disambiguationData":[OSD([sQuery(id+"F7.wireOp",EDGE,"E18")])],"isStart":false});
            revolve(context, id + "F20", {"entities" : qUnion([Q0]), "axis" : qUnion([Q1]), "revolveType" : RevolveType.FULL});
        }
    });
